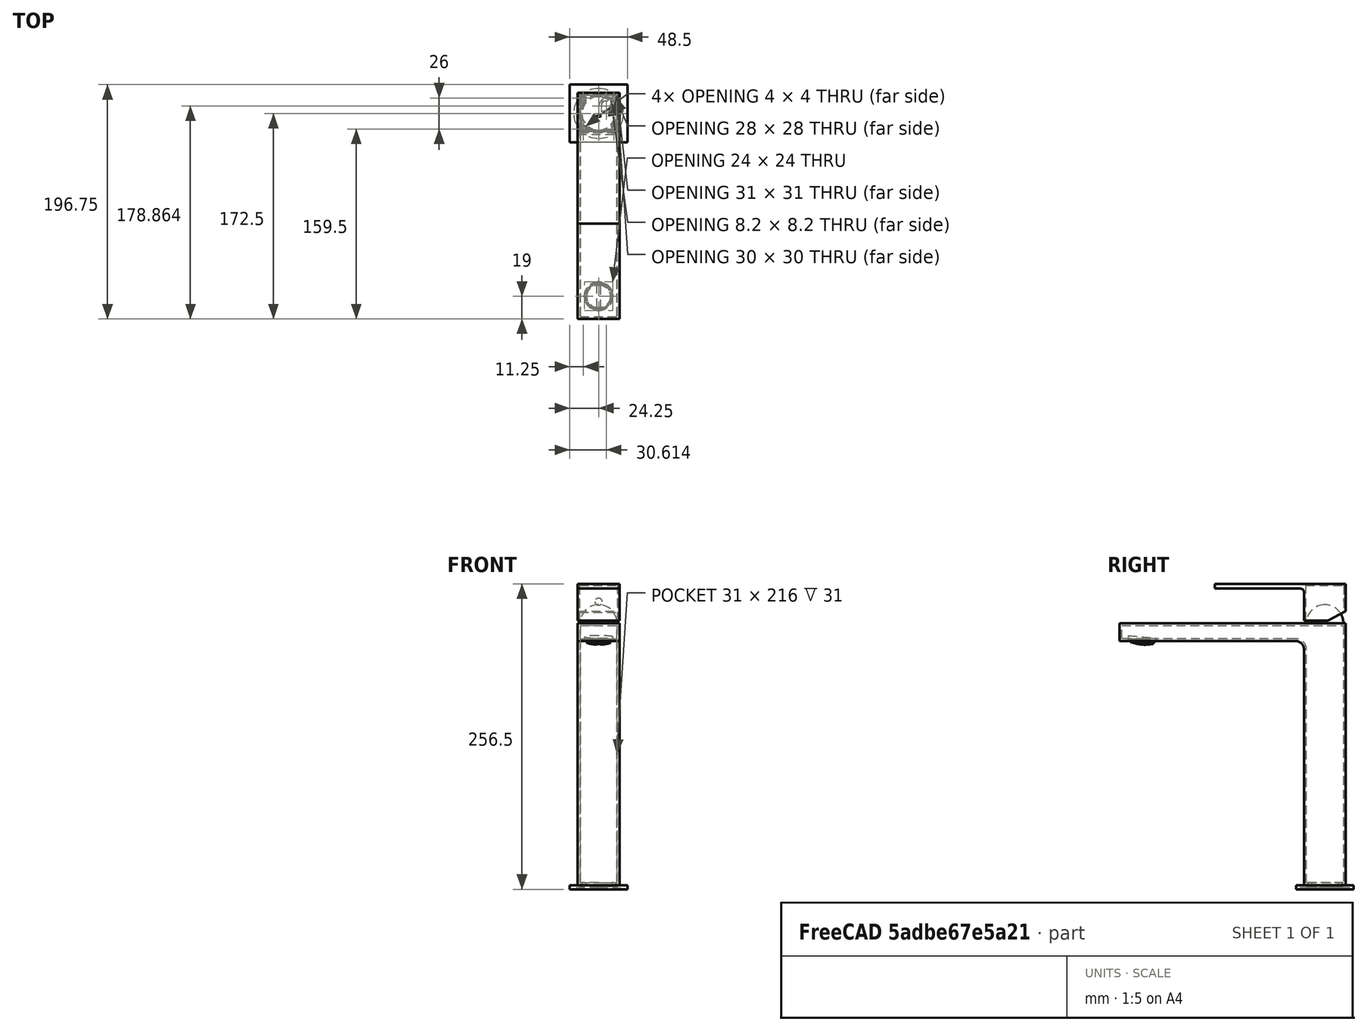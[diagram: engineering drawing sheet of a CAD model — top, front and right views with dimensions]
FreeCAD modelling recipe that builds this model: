
FCSTD DOCUMENT  (FreeCAD 1.0R38641 +468 (Git))
Label: Faucet_Unitas
License: All rights reserved
objects: Part::Feature×1, Part::FeaturePython×1
note: 2 computed .brp shape members not serialized (recipe doc carries the construction recipe); baked Part::Feature solids carry a one-line shape summary decoded from their .brp

FEATURE [Part::Feature] Compound  label="Model of Faucet Unitas"
  Placement = pos=(0,0,0) rot=(0,0.707107,0.707107;3.14159rad)
  shape: bbox 48.5 x 196.8 x 256.5 mm, 235 faces, 4 solids (baked)
FEATURE [Part::FeaturePython] Component  label="Faucet_Unitas"  # Arch/BIM 22 (typed FeaturePython)
  Base = -> Compound
  Description = Faucet Unitas
  HorizontalArea = 0
  IfcData = attributes={"GlobalId": {"name": "GlobalId", "type": "IfcGloballyUniqueId", "is_enum": false, "enum_values": []}, "Description": {"... (+564 chars omitted),+1 more (map truncated)
  IfcType = 22
  MoveBase = false
  MoveWithHost = false
  PerimeterLength = 0
  Placement = pos=(0,0,0) rot=(0,0.707107,0.707107;3.14159rad)
  VerticalArea = 0
